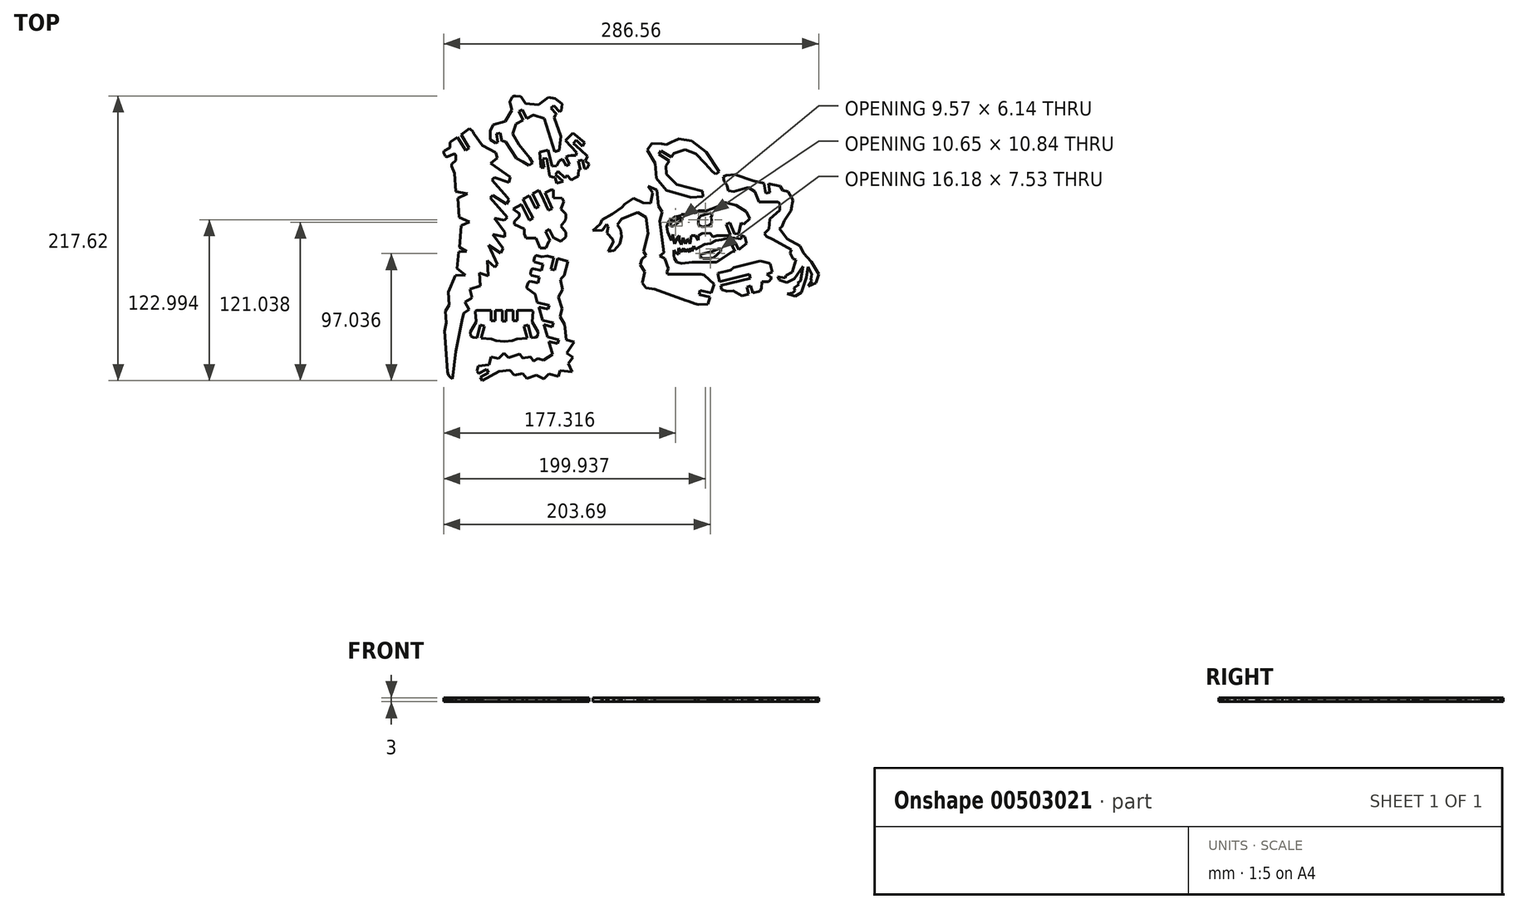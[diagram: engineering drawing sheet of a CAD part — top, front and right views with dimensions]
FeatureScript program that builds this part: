
annotation { "Feature Type Name" : "Feature", "Feature Type Description" : "" }
export const myFeature = defineFeature(function(context is Context, id is Id, definition is map)
    precondition{}
    {
        {
            var Q0;
            Q0=qCreatedBy(makeId("Top.planeOp"),FACE);
            var sketch = newSketch(context, id + "F0", { "sketchPlane" : qUnion([Q0])});
            skLineSegment(sketch, "E0", {"start": v(91.5, -36.51) * mm, "end": v(92.84, -41.9) * mm});
            skLineSegment(sketch, "E1", {"start": v(88.49, -37.26) * mm, "end": v(91.5, -36.51) * mm});
            skLineSegment(sketch, "E2", {"start": v(89.88, -42.83) * mm, "end": v(88.49, -37.26) * mm});
            skLineSegment(sketch, "E3", {"start": v(84.64, -44.14) * mm, "end": v(89.88, -42.83) * mm});
            skLineSegment(sketch, "E4", {"start": v(77.97, -40.13) * mm, "end": v(84.64, -44.14) * mm});
            skLineSegment(sketch, "E5", {"start": v(73.4, -40.63) * mm, "end": v(77.97, -40.13) * mm});
            skLineSegment(sketch, "E6", {"start": v(69.24, -39.21) * mm, "end": v(73.4, -40.63) * mm});
            skLineSegment(sketch, "E7", {"start": v(68.48, -36.17) * mm, "end": v(69.24, -39.21) * mm});
            skLineSegment(sketch, "E8", {"start": v(91.02, -30.55) * mm, "end": v(68.48, -36.17) * mm});
            skLineSegment(sketch, "E9", {"start": v(90.27, -27.54) * mm, "end": v(91.02, -30.55) * mm});
            skLineSegment(sketch, "E10", {"start": v(67.7, -33.17) * mm, "end": v(90.27, -27.54) * mm});
            skLineSegment(sketch, "E11", {"start": v(66.21, -27.25) * mm, "end": v(67.7, -33.17) * mm});
            skLineSegment(sketch, "E12", {"start": v(11.35, -37.86) * mm, "end": v(18.08, -38.98) * mm});
            skLineSegment(sketch, "E13", {"start": v(8.5, -34.14) * mm, "end": v(11.35, -37.86) * mm});
            skLineSegment(sketch, "E14", {"start": v(10.51, -25.54) * mm, "end": v(8.5, -34.14) * mm});
            skLineSegment(sketch, "E15", {"start": v(6.82, -20.1) * mm, "end": v(10.51, -25.54) * mm});
            skLineSegment(sketch, "E16", {"start": v(8.26, -16.25) * mm, "end": v(6.82, -20.1) * mm});
            skLineSegment(sketch, "E17", {"start": v(11.39, -13.12) * mm, "end": v(8.26, -16.25) * mm});
            skLineSegment(sketch, "E18", {"start": v(9.35, -10.1) * mm, "end": v(11.39, -13.12) * mm});
            skLineSegment(sketch, "E19", {"start": v(12.95, 3.58) * mm, "end": v(9.35, -10.1) * mm});
            skLineSegment(sketch, "E20", {"start": v(11.44, 15.91) * mm, "end": v(12.95, 3.58) * mm});
            skLineSegment(sketch, "E21", {"start": v(5.16, 19.64) * mm, "end": v(11.44, 15.91) * mm});
            skLineSegment(sketch, "E22", {"start": v(-7.45, 14.69) * mm, "end": v(5.16, 19.64) * mm});
            skLineSegment(sketch, "E23", {"start": v(-10.52, 10.32) * mm, "end": v(-7.45, 14.69) * mm});
            skLineSegment(sketch, "E24", {"start": v(-7.95, 6.53) * mm, "end": v(-10.52, 10.32) * mm});
            skLineSegment(sketch, "E25", {"start": v(-7.5, 1.3) * mm, "end": v(-7.95, 6.53) * mm});
            skLineSegment(sketch, "E26", {"start": v(-8.77, -4.3) * mm, "end": v(-7.5, 1.3) * mm});
            skLineSegment(sketch, "E27", {"start": v(-13.03, -9.3) * mm, "end": v(-8.77, -4.3) * mm});
            skLineSegment(sketch, "E28", {"start": v(-17.48, -10.2) * mm, "end": v(-13.03, -9.3) * mm});
            skLineSegment(sketch, "E29", {"start": v(-13.87, -3.02) * mm, "end": v(-17.48, -10.2) * mm});
            skLineSegment(sketch, "E30", {"start": v(-14.1, -0.74) * mm, "end": v(-13.87, -3.02) * mm});
            skLineSegment(sketch, "E31", {"start": v(-18.63, 4.02) * mm, "end": v(-14.1, -0.74) * mm});
            skLineSegment(sketch, "E32", {"start": v(-17.58, 8.96) * mm, "end": v(-18.63, 4.02) * mm});
            skLineSegment(sketch, "E33", {"start": v(-18.72, 10.64) * mm, "end": v(-17.58, 8.96) * mm});
            skLineSegment(sketch, "E34", {"start": v(-21.94, 6.01) * mm, "end": v(-18.72, 10.64) * mm});
            skLineSegment(sketch, "E35", {"start": v(-29.34, 5.88) * mm, "end": v(-21.94, 6.01) * mm});
            skLineSegment(sketch, "E36", {"start": v(-23.62, 10.9) * mm, "end": v(-29.34, 5.88) * mm});
            skLineSegment(sketch, "E37", {"start": v(-22.26, 13.94) * mm, "end": v(-23.62, 10.9) * mm});
            skLineSegment(sketch, "E38", {"start": v(-14.4, 18.45) * mm, "end": v(-22.26, 13.94) * mm});
            skLineSegment(sketch, "E39", {"start": v(-7.03, 23.44) * mm, "end": v(-14.4, 18.45) * mm});
            skLineSegment(sketch, "E40", {"start": v(-4.88, 26.04) * mm, "end": v(-7.03, 23.44) * mm});
            skLineSegment(sketch, "E41", {"start": v(1.71, 30.5) * mm, "end": v(-4.88, 26.04) * mm});
            skLineSegment(sketch, "E42", {"start": v(9, 26.97) * mm, "end": v(1.71, 30.5) * mm});
            skLineSegment(sketch, "E43", {"start": v(14.87, 26.71) * mm, "end": v(9, 26.97) * mm});
            skLineSegment(sketch, "E44", {"start": v(16.42, 34.77) * mm, "end": v(14.87, 26.71) * mm});
            skLineSegment(sketch, "E45", {"start": v(13.02, 39.8) * mm, "end": v(16.42, 34.77) * mm});
            skLineSegment(sketch, "E46", {"start": v(19.66, 36.96) * mm, "end": v(13.02, 39.8) * mm});
            skLineSegment(sketch, "E47", {"start": v(20.84, 24.4) * mm, "end": v(19.66, 36.96) * mm});
            skLineSegment(sketch, "E48", {"start": v(23.71, 20.16) * mm, "end": v(20.84, 24.4) * mm});
            skLineSegment(sketch, "E49", {"start": v(21.75, 12.96) * mm, "end": v(23.71, 20.16) * mm});
            skLineSegment(sketch, "E50", {"start": v(25.16, -11.09) * mm, "end": v(21.75, 12.96) * mm});
            skLineSegment(sketch, "E51", {"start": v(21.7, -13.43) * mm, "end": v(25.16, -11.09) * mm});
            skLineSegment(sketch, "E52", {"start": v(25.79, -15.33) * mm, "end": v(21.7, -13.43) * mm});
            skLineSegment(sketch, "E53", {"start": v(28.42, -23.51) * mm, "end": v(25.79, -15.33) * mm});
            skLineSegment(sketch, "E54", {"start": v(27.1, -25.68) * mm, "end": v(28.42, -23.51) * mm});
            skLineSegment(sketch, "E55", {"start": v(27.94, -27.41) * mm, "end": v(27.1, -25.68) * mm});
            skLineSegment(sketch, "E56", {"start": v(53.26, -27.63) * mm, "end": v(27.94, -27.41) * mm});
            skLineSegment(sketch, "E57", {"start": v(66.5, -26.64) * mm, "end": v(66.21, -27.25) * mm});
            skLineSegment(sketch, "E58", {"start": v(78.2, -22.41) * mm, "end": v(75.97, -24.28) * mm});
            skLineSegment(sketch, "E59", {"start": v(98.62, -17.32) * mm, "end": v(78.2, -22.41) * mm});
            skLineSegment(sketch, "E60", {"start": v(105.1, -18.96) * mm, "end": v(98.62, -17.32) * mm});
            skLineSegment(sketch, "E61", {"start": v(106.28, -19.5) * mm, "end": v(105.1, -18.96) * mm});
            skLineSegment(sketch, "E62", {"start": v(107.87, -25.84) * mm, "end": v(106.28, -19.5) * mm});
            skLineSegment(sketch, "E63", {"start": v(103.89, -27.41) * mm, "end": v(107.87, -25.84) * mm});
            skLineSegment(sketch, "E64", {"start": v(107.45, -30.37) * mm, "end": v(103.89, -27.41) * mm});
            skLineSegment(sketch, "E65", {"start": v(105.05, -33.27) * mm, "end": v(107.45, -30.37) * mm});
            skLineSegment(sketch, "E66", {"start": v(100.07, -33.14) * mm, "end": v(105.05, -33.27) * mm});
            skLineSegment(sketch, "E67", {"start": v(99.76, -38.45) * mm, "end": v(100.07, -33.14) * mm});
            skLineSegment(sketch, "E68", {"start": v(98.24, -40.54) * mm, "end": v(99.76, -38.45) * mm});
            skLineSegment(sketch, "E69", {"start": v(92.84, -41.9) * mm, "end": v(98.24, -40.54) * mm});
            skLineSegment(sketch, "E70", {"start": v(-40.32, 47.37) * mm, "end": v(-40.32, 48.76) * mm});
            skLineSegment(sketch, "E71", {"start": v(-49.1, 48.05) * mm, "end": v(-45.64, 44.43) * mm});
            skLineSegment(sketch, "E72", {"start": v(-50.47, 46.1) * mm, "end": v(-49.1, 48.05) * mm});
            skLineSegment(sketch, "E73", {"start": v(-55.93, 51.06) * mm, "end": v(-50.47, 46.1) * mm});
            skLineSegment(sketch, "E74", {"start": v(-58.02, 48.77) * mm, "end": v(-55.93, 51.06) * mm});
            skLineSegment(sketch, "E75", {"start": v(-52.27, 43.55) * mm, "end": v(-58.02, 48.77) * mm});
            skLineSegment(sketch, "E76", {"start": v(-52.48, 43.26) * mm, "end": v(-52.27, 43.55) * mm});
            skLineSegment(sketch, "E77", {"start": v(-57, 42.03) * mm, "end": v(-52.48, 43.26) * mm});
            skLineSegment(sketch, "E78", {"start": v(-58.2, 46.42) * mm, "end": v(-57, 42.03) * mm});
            skLineSegment(sketch, "E79", {"start": v(-59.97, 46.65) * mm, "end": v(-58.2, 46.42) * mm});
            skLineSegment(sketch, "E80", {"start": v(-59.95, 46.62) * mm, "end": v(-59.97, 46.65) * mm});
            skLineSegment(sketch, "E81", {"start": v(-62.16, 47.52) * mm, "end": v(-59.95, 46.62) * mm});
            skLineSegment(sketch, "E82", {"start": v(-64.51, 61.19) * mm, "end": v(-62.16, 47.52) * mm});
            skLineSegment(sketch, "E83", {"start": v(-67.57, 60.67) * mm, "end": v(-64.51, 61.19) * mm});
            skLineSegment(sketch, "E84", {"start": v(-66.45, 54.1) * mm, "end": v(-67.57, 60.67) * mm});
            skLineSegment(sketch, "E85", {"start": v(-69.05, 53.91) * mm, "end": v(-66.45, 54.1) * mm});
            skLineSegment(sketch, "E86", {"start": v(-69.9, 65.77) * mm, "end": v(-69.05, 53.91) * mm});
            skLineSegment(sketch, "E87", {"start": v(-63.55, 67.35) * mm, "end": v(-69.9, 65.77) * mm});
            skLineSegment(sketch, "E88", {"start": v(-60.5, 55.1) * mm, "end": v(-63.55, 67.35) * mm});
            skLineSegment(sketch, "E89", {"start": v(-56.93, 55.35) * mm, "end": v(-60.5, 55.1) * mm});
            skLineSegment(sketch, "E90", {"start": v(-55.15, 59.04) * mm, "end": v(-56.93, 55.35) * mm});
            skLineSegment(sketch, "E91", {"start": v(-52.61, 60.44) * mm, "end": v(-55.15, 59.04) * mm});
            skLineSegment(sketch, "E92", {"start": v(-49.76, 55.27) * mm, "end": v(-52.61, 60.44) * mm});
            skLineSegment(sketch, "E93", {"start": v(-47.05, 56.76) * mm, "end": v(-49.76, 55.27) * mm});
            skLineSegment(sketch, "E94", {"start": v(-49.9, 61.94) * mm, "end": v(-47.05, 56.76) * mm});
            skLineSegment(sketch, "E95", {"start": v(-48.13, 62.91) * mm, "end": v(-49.9, 61.94) * mm});
            skLineSegment(sketch, "E96", {"start": v(-48.13, 62.91) * mm, "end": v(-46.1, 63.33) * mm});
            skLineSegment(sketch, "E97", {"start": v(-42.38, 63.37) * mm, "end": v(-46.1, 63.33) * mm});
            skLineSegment(sketch, "E98", {"start": v(-41.79, 65.42) * mm, "end": v(-42.38, 63.37) * mm});
            skLineSegment(sketch, "E99", {"start": v(-50.23, 74.7) * mm, "end": v(-41.79, 65.42) * mm});
            skLineSegment(sketch, "E100", {"start": v(-44.68, 80.27) * mm, "end": v(-50.23, 74.7) * mm});
            skLineSegment(sketch, "E101", {"start": v(-35.65, 73) * mm, "end": v(-44.68, 80.27) * mm});
            skLineSegment(sketch, "E102", {"start": v(-37.16, 70.38) * mm, "end": v(-35.65, 73) * mm});
            skLineSegment(sketch, "E103", {"start": v(-42, 74.87) * mm, "end": v(-37.16, 70.38) * mm});
            skLineSegment(sketch, "E104", {"start": v(-44.11, 72.6) * mm, "end": v(-42, 74.87) * mm});
            skLineSegment(sketch, "E105", {"start": v(-38.76, 67.64) * mm, "end": v(-44.11, 72.6) * mm});
            skLineSegment(sketch, "E106", {"start": v(-33.5, 62.57) * mm, "end": v(-38.76, 67.64) * mm});
            skLineSegment(sketch, "E107", {"start": v(-34.9, 59.27) * mm, "end": v(-33.5, 62.57) * mm});
            skLineSegment(sketch, "E108", {"start": v(-32.13, 56.54) * mm, "end": v(-34.9, 59.27) * mm});
            skLineSegment(sketch, "E109", {"start": v(-33.8, 53.56) * mm, "end": v(-32.13, 56.54) * mm});
            skLineSegment(sketch, "E110", {"start": v(-35.68, 53) * mm, "end": v(-33.8, 53.56) * mm});
            skLineSegment(sketch, "E111", {"start": v(-37.22, 59.76) * mm, "end": v(-35.68, 53) * mm});
            skLineSegment(sketch, "E112", {"start": v(-40.24, 59.08) * mm, "end": v(-37.22, 59.76) * mm});
            skLineSegment(sketch, "E113", {"start": v(-38.66, 52.13) * mm, "end": v(-40.24, 59.08) * mm});
            skLineSegment(sketch, "E114", {"start": v(-38.75, 52.1) * mm, "end": v(-38.66, 52.13) * mm});
            skLineSegment(sketch, "E115", {"start": v(-40.04, 52.33) * mm, "end": v(-38.75, 52.1) * mm});
            skLineSegment(sketch, "E116", {"start": v(-53.83, 9.3) * mm, "end": v(-50.26, 13.88) * mm});
            skLineSegment(sketch, "E117", {"start": v(-50.05, 4.57) * mm, "end": v(-53.83, 9.3) * mm});
            skLineSegment(sketch, "E118", {"start": v(-50.05, 0.93) * mm, "end": v(-50.05, 4.57) * mm});
            skLineSegment(sketch, "E119", {"start": v(-53.83, -2.31) * mm, "end": v(-50.05, 0.93) * mm});
            skLineSegment(sketch, "E120", {"start": v(-58.95, -0.02) * mm, "end": v(-53.83, -2.31) * mm});
            skLineSegment(sketch, "E121", {"start": v(-59.24, -0.19) * mm, "end": v(-58.95, -0.02) * mm});
            skLineSegment(sketch, "E122", {"start": v(-62.65, 6.68) * mm, "end": v(-59.24, -0.19) * mm});
            skLineSegment(sketch, "E123", {"start": v(-65.43, 5.3) * mm, "end": v(-62.65, 6.68) * mm});
            skLineSegment(sketch, "E124", {"start": v(-61.92, -1.76) * mm, "end": v(-65.43, 5.3) * mm});
            skLineSegment(sketch, "E125", {"start": v(-62.86, -2.31) * mm, "end": v(-61.92, -1.76) * mm});
            skLineSegment(sketch, "E126", {"start": v(-65.16, -7.44) * mm, "end": v(-62.86, -2.31) * mm});
            skLineSegment(sketch, "E127", {"start": v(-69.74, -7.44) * mm, "end": v(-65.16, -7.44) * mm});
            skLineSegment(sketch, "E128", {"start": v(-72.85, -0.02) * mm, "end": v(-69.74, -7.44) * mm});
            skLineSegment(sketch, "E129", {"start": v(-81.75, 3.35) * mm, "end": v(-80.53, -0.02) * mm});
            skLineSegment(sketch, "E130", {"start": v(-81.75, 7.13) * mm, "end": v(-81.75, 3.35) * mm});
            skLineSegment(sketch, "E131", {"start": v(-95.51, -63.25) * mm, "end": v(-98.62, -63.25) * mm});
            skLineSegment(sketch, "E132", {"start": v(-95.51, -55.05) * mm, "end": v(-95.51, -63.25) * mm});
            skLineSegment(sketch, "E133", {"start": v(-90.16, -55.05) * mm, "end": v(-95.51, -55.05) * mm});
            skLineSegment(sketch, "E134", {"start": v(-90.16, -63.23) * mm, "end": v(-90.16, -55.05) * mm});
            skLineSegment(sketch, "E135", {"start": v(-87.05, -63.23) * mm, "end": v(-90.16, -63.23) * mm});
            skLineSegment(sketch, "E136", {"start": v(-87.05, -55.05) * mm, "end": v(-87.05, -63.23) * mm});
            skLineSegment(sketch, "E137", {"start": v(-76.28, -55.05) * mm, "end": v(-87.05, -55.05) * mm});
            skLineSegment(sketch, "E138", {"start": v(-75.04, -55.83) * mm, "end": v(-76.28, -55.05) * mm});
            skLineSegment(sketch, "E139", {"start": v(-75.48, -63.94) * mm, "end": v(-75.04, -55.83) * mm});
            skLineSegment(sketch, "E140", {"start": v(-71.21, -71.63) * mm, "end": v(-75.48, -63.94) * mm});
            skLineSegment(sketch, "E141", {"start": v(-71.65, -74.71) * mm, "end": v(-71.21, -71.63) * mm});
            skLineSegment(sketch, "E142", {"start": v(-73.26, -75.84) * mm, "end": v(-71.65, -74.71) * mm});
            skLineSegment(sketch, "E143", {"start": v(-76.36, -76.12) * mm, "end": v(-73.26, -75.84) * mm});
            skLineSegment(sketch, "E144", {"start": v(-78.83, -66.37) * mm, "end": v(-76.36, -76.12) * mm});
            skLineSegment(sketch, "E145", {"start": v(-81.84, -67.13) * mm, "end": v(-78.83, -66.37) * mm});
            skLineSegment(sketch, "E146", {"start": v(-79.48, -76.4) * mm, "end": v(-81.84, -67.13) * mm});
            skLineSegment(sketch, "E147", {"start": v(-87.36, -77.1) * mm, "end": v(-79.48, -76.4) * mm});
            skLineSegment(sketch, "E148", {"start": v(-89.17, 10.64) * mm, "end": v(-81.75, 7.13) * mm});
            skLineSegment(sketch, "E149", {"start": v(-89.17, 12.66) * mm, "end": v(-89.17, 10.64) * mm});
            skLineSegment(sketch, "E150", {"start": v(-85.39, 16.57) * mm, "end": v(-89.17, 12.66) * mm});
            skLineSegment(sketch, "E151", {"start": v(-85.39, 18.87) * mm, "end": v(-85.39, 16.57) * mm});
            skLineSegment(sketch, "E152", {"start": v(-90.38, 22.24) * mm, "end": v(-85.39, 18.87) * mm});
            skLineSegment(sketch, "E153", {"start": v(-83.99, 25.73) * mm, "end": v(-90.38, 22.24) * mm});
            skLineSegment(sketch, "E154", {"start": v(-77.85, 13.83) * mm, "end": v(-83.99, 25.73) * mm});
            skLineSegment(sketch, "E155", {"start": v(-75.1, 15.25) * mm, "end": v(-77.85, 13.83) * mm});
            skLineSegment(sketch, "E156", {"start": v(-81.27, 27.22) * mm, "end": v(-75.1, 15.25) * mm});
            skLineSegment(sketch, "E157", {"start": v(-82.76, 29.95) * mm, "end": v(-81.27, 27.22) * mm});
            skLineSegment(sketch, "E158", {"start": v(-77.93, 32.6) * mm, "end": v(-82.76, 29.95) * mm});
            skLineSegment(sketch, "E159", {"start": v(-73.19, 22.97) * mm, "end": v(-77.93, 32.6) * mm});
            skLineSegment(sketch, "E160", {"start": v(-70.4, 24.34) * mm, "end": v(-73.19, 22.97) * mm});
            skLineSegment(sketch, "E161", {"start": v(-75.2, 34.09) * mm, "end": v(-70.4, 24.34) * mm});
            skLineSegment(sketch, "E162", {"start": v(-70.59, 36.61) * mm, "end": v(-75.2, 34.09) * mm});
            skLineSegment(sketch, "E163", {"start": v(-68.67, 33.1) * mm, "end": v(-70.59, 36.61) * mm});
            skLineSegment(sketch, "E164", {"start": v(-63.22, 21.21) * mm, "end": v(-68.67, 33.1) * mm});
            skLineSegment(sketch, "E165", {"start": v(-60.4, 22.5) * mm, "end": v(-63.22, 21.21) * mm});
            skLineSegment(sketch, "E166", {"start": v(-65.94, 34.59) * mm, "end": v(-60.4, 22.5) * mm});
            skLineSegment(sketch, "E167", {"start": v(-61.45, 37.04) * mm, "end": v(-65.94, 34.59) * mm});
            skLineSegment(sketch, "E168", {"start": v(-59.5, 37.04) * mm, "end": v(-61.45, 37.04) * mm});
            skLineSegment(sketch, "E169", {"start": v(-59.5, 31) * mm, "end": v(-59.5, 37.04) * mm});
            skLineSegment(sketch, "E170", {"start": v(-52.88, 30.6) * mm, "end": v(-59.5, 31) * mm});
            skLineSegment(sketch, "E171", {"start": v(-51.4, 27.9) * mm, "end": v(-52.88, 30.6) * mm});
            skLineSegment(sketch, "E172", {"start": v(-50.05, 18.6) * mm, "end": v(-53.83, 22.37) * mm});
            skLineSegment(sketch, "E173", {"start": v(-50.05, 16.1) * mm, "end": v(-50.05, 18.6) * mm});
            skLineSegment(sketch, "E174", {"start": v(122.4, -8.86) * mm, "end": v(121.6, -11.43) * mm});
            skLineSegment(sketch, "E175", {"start": v(108.16, -1) * mm, "end": v(122.4, -8.86) * mm});
            skLineSegment(sketch, "E176", {"start": v(103.31, 1.25) * mm, "end": v(108.16, -1) * mm});
            skLineSegment(sketch, "E177", {"start": v(101.98, 3.56) * mm, "end": v(103.31, 1.25) * mm});
            skLineSegment(sketch, "E178", {"start": v(105.23, 7.2) * mm, "end": v(101.98, 3.56) * mm});
            skLineSegment(sketch, "E179", {"start": v(105.81, 14.67) * mm, "end": v(105.23, 7.2) * mm});
            skLineSegment(sketch, "E180", {"start": v(113.73, 21.48) * mm, "end": v(105.81, 14.67) * mm});
            skLineSegment(sketch, "E181", {"start": v(113.63, 26.45) * mm, "end": v(113.73, 21.48) * mm});
            skLineSegment(sketch, "E182", {"start": v(112.42, 27.72) * mm, "end": v(113.63, 26.45) * mm});
            skLineSegment(sketch, "E183", {"start": v(97.73, 27.84) * mm, "end": v(112.42, 27.72) * mm});
            skLineSegment(sketch, "E184", {"start": v(102.92, 34.46) * mm, "end": v(105.98, 34.97) * mm});
            skLineSegment(sketch, "E185", {"start": v(-89.68, 108.64) * mm, "end": v(-90.25, 108.36) * mm});
            skLineSegment(sketch, "E186", {"start": v(-89.06, 108.81) * mm, "end": v(-89.68, 108.64) * mm});
            skLineSegment(sketch, "E187", {"start": v(-88.42, 108.68) * mm, "end": v(-89.06, 108.81) * mm});
            skLineSegment(sketch, "E188", {"start": v(-84.61, 108.24) * mm, "end": v(-88.42, 108.68) * mm});
            skLineSegment(sketch, "E189", {"start": v(-84.21, 107.97) * mm, "end": v(-84.61, 108.24) * mm});
            skLineSegment(sketch, "E190", {"start": v(-83.93, 107.57) * mm, "end": v(-84.21, 107.97) * mm});
            skLineSegment(sketch, "E191", {"start": v(-80.83, 102.96) * mm, "end": v(-83.93, 107.57) * mm});
            skLineSegment(sketch, "E192", {"start": v(-70.9, 102) * mm, "end": v(-80.83, 102.96) * mm});
            skLineSegment(sketch, "E193", {"start": v(-59.22, 101.52) * mm, "end": v(-61.49, 99.4) * mm});
            skLineSegment(sketch, "E194", {"start": v(-54.48, 103.9) * mm, "end": v(-58.15, 106.62) * mm});
            skLineSegment(sketch, "E195", {"start": v(-53.38, 97.7) * mm, "end": v(-52.85, 102.69) * mm});
            skLineSegment(sketch, "E196", {"start": v(-57.72, 94.48) * mm, "end": v(-57.23, 94.84) * mm});
            skLineSegment(sketch, "E197", {"start": v(-58.81, 92.13) * mm, "end": v(-57.72, 94.48) * mm});
            skLineSegment(sketch, "E198", {"start": v(36.44, 76.04) * mm, "end": v(46.32, 74.24) * mm});
            skLineSegment(sketch, "E199", {"start": v(46.32, 74.24) * mm, "end": v(57.28, 65.88) * mm});
            skLineSegment(sketch, "E200", {"start": v(67.26, 51) * mm, "end": v(57.28, 65.88) * mm});
            skLineSegment(sketch, "E201", {"start": v(64.6, 48.91) * mm, "end": v(67.26, 51) * mm});
            skLineSegment(sketch, "E202", {"start": v(62.1, 50.83) * mm, "end": v(64.6, 48.91) * mm});
            skLineSegment(sketch, "E203", {"start": v(56.57, 57.27) * mm, "end": v(62.1, 50.83) * mm});
            skLineSegment(sketch, "E204", {"start": v(49.55, 64.5) * mm, "end": v(56.57, 57.27) * mm});
            skLineSegment(sketch, "E205", {"start": v(41.34, 67.72) * mm, "end": v(49.55, 64.5) * mm});
            skLineSegment(sketch, "E206", {"start": v(32.54, 64.95) * mm, "end": v(41.34, 67.72) * mm});
            skLineSegment(sketch, "E207", {"start": v(30.64, 61.92) * mm, "end": v(32.54, 64.95) * mm});
            skLineSegment(sketch, "E208", {"start": v(22.94, 66.76) * mm, "end": v(30.64, 61.92) * mm});
            skLineSegment(sketch, "E209", {"start": v(21.29, 64.14) * mm, "end": v(22.94, 66.76) * mm});
            skLineSegment(sketch, "E210", {"start": v(28.99, 59.3) * mm, "end": v(21.29, 64.14) * mm});
            skLineSegment(sketch, "E211", {"start": v(26.51, 55.36) * mm, "end": v(28.99, 59.3) * mm});
            skLineSegment(sketch, "E212", {"start": v(27.04, 48.98) * mm, "end": v(26.51, 55.36) * mm});
            skLineSegment(sketch, "E213", {"start": v(34.95, 41.07) * mm, "end": v(27.04, 48.98) * mm});
            skLineSegment(sketch, "E214", {"start": v(54.59, 36) * mm, "end": v(34.95, 41.07) * mm});
            skLineSegment(sketch, "E215", {"start": v(54.89, 31.77) * mm, "end": v(54.59, 36) * mm});
            skLineSegment(sketch, "E216", {"start": v(45.66, 31.14) * mm, "end": v(54.89, 31.77) * mm});
            skLineSegment(sketch, "E217", {"start": v(26.77, 36.65) * mm, "end": v(45.66, 31.14) * mm});
            skLineSegment(sketch, "E218", {"start": v(19.16, 45.73) * mm, "end": v(26.77, 36.65) * mm});
            skLineSegment(sketch, "E219", {"start": v(18.4, 57.33) * mm, "end": v(19.16, 45.73) * mm});
            skLineSegment(sketch, "E220", {"start": v(12.39, 67.49) * mm, "end": v(18.4, 57.33) * mm});
            skLineSegment(sketch, "E221", {"start": v(15.7, 72.51) * mm, "end": v(12.39, 67.49) * mm});
            skLineSegment(sketch, "E222", {"start": v(23.45, 72.05) * mm, "end": v(15.7, 72.51) * mm});
            skLineSegment(sketch, "E223", {"start": v(-53.75, 77.9) * mm, "end": v(-58.81, 92.13) * mm});
            skLineSegment(sketch, "E224", {"start": v(-55.12, 67.1) * mm, "end": v(-53.75, 77.9) * mm});
            skLineSegment(sketch, "E225", {"start": v(-58.37, 66) * mm, "end": v(-55.12, 67.1) * mm});
            skLineSegment(sketch, "E226", {"start": v(-74.91, 93.93) * mm, "end": v(-74.24, 94.08) * mm});
            skLineSegment(sketch, "E227", {"start": v(-79.87, 91.63) * mm, "end": v(-74.91, 93.93) * mm});
            skLineSegment(sketch, "E228", {"start": v(-83.17, 98.27) * mm, "end": v(-79.87, 91.63) * mm});
            skLineSegment(sketch, "E229", {"start": v(94.59, 35.58) * mm, "end": v(97.73, 27.84) * mm});
            skLineSegment(sketch, "E230", {"start": v(89.5, 38.72) * mm, "end": v(94.59, 35.58) * mm});
            skLineSegment(sketch, "E231", {"start": v(78.35, 35.58) * mm, "end": v(89.5, 38.72) * mm});
            skLineSegment(sketch, "E232", {"start": v(73.4, 40.45) * mm, "end": v(74.12, 36.16) * mm});
            skLineSegment(sketch, "E233", {"start": v(-93.53, 42.69) * mm, "end": v(-92.32, 46.63) * mm});
            skLineSegment(sketch, "E234", {"start": v(-104.44, 46.56) * mm, "end": v(-93.53, 42.69) * mm});
            skLineSegment(sketch, "E235", {"start": v(-106.5, 44.53) * mm, "end": v(-104.44, 46.56) * mm});
            skLineSegment(sketch, "E236", {"start": v(-94.8, 31.36) * mm, "end": v(-106.5, 44.53) * mm});
            skLineSegment(sketch, "E237", {"start": v(-95.24, 26.04) * mm, "end": v(-93.45, 29.23) * mm});
            skLineSegment(sketch, "E238", {"start": v(-105.73, 32.84) * mm, "end": v(-95.24, 26.04) * mm});
            skLineSegment(sketch, "E239", {"start": v(-107.6, 30.94) * mm, "end": v(-105.73, 32.84) * mm});
            skLineSegment(sketch, "E240", {"start": v(-94.58, 16.08) * mm, "end": v(-107.6, 30.94) * mm});
            skLineSegment(sketch, "E241", {"start": v(-96.76, 13.87) * mm, "end": v(-94.58, 16.08) * mm});
            skLineSegment(sketch, "E242", {"start": v(-104.59, 15.32) * mm, "end": v(-96.76, 13.87) * mm});
            skLineSegment(sketch, "E243", {"start": v(-96.68, 4.47) * mm, "end": v(-104.59, 15.32) * mm});
            skLineSegment(sketch, "E244", {"start": v(-96.45, 1.07) * mm, "end": v(-96.68, 4.47) * mm});
            skLineSegment(sketch, "E245", {"start": v(-105.77, 2.94) * mm, "end": v(-96.45, 1.07) * mm});
            skLineSegment(sketch, "E246", {"start": v(-97.78, -7.99) * mm, "end": v(-105.77, 2.94) * mm});
            skLineSegment(sketch, "E247", {"start": v(-99.76, -11.39) * mm, "end": v(-97.78, -7.99) * mm});
            skLineSegment(sketch, "E248", {"start": v(-108.83, -5.25) * mm, "end": v(-99.76, -11.39) * mm});
            skLineSegment(sketch, "E249", {"start": v(-102.29, -19.82) * mm, "end": v(-108.83, -5.25) * mm});
            skLineSegment(sketch, "E250", {"start": v(-104.13, -22.19) * mm, "end": v(-102.29, -19.82) * mm});
            skLineSegment(sketch, "E251", {"start": v(-109.96, -16.94) * mm, "end": v(-104.13, -22.19) * mm});
            skLineSegment(sketch, "E252", {"start": v(-109.2, -28.71) * mm, "end": v(-109.96, -16.94) * mm});
            skLineSegment(sketch, "E253", {"start": v(-115.82, -26.49) * mm, "end": v(-109.2, -28.71) * mm});
            skLineSegment(sketch, "E254", {"start": v(-115.18, -36.28) * mm, "end": v(-115.82, -26.49) * mm});
            skLineSegment(sketch, "E255", {"start": v(-123.32, -38.89) * mm, "end": v(-115.18, -36.28) * mm});
            skLineSegment(sketch, "E256", {"start": v(-121.55, -45.3) * mm, "end": v(-123.32, -38.89) * mm});
            skLineSegment(sketch, "E257", {"start": v(-127.1, -48.96) * mm, "end": v(-122.8, -46.4) * mm});
            skLineSegment(sketch, "E258", {"start": v(-124, -54.4) * mm, "end": v(-127.1, -48.96) * mm});
            skLineSegment(sketch, "E259", {"start": v(-128.02, -57.45) * mm, "end": v(-124, -54.4) * mm});
            skLineSegment(sketch, "E260", {"start": v(-129.31, -62.86) * mm, "end": v(-128.02, -57.45) * mm});
            skLineSegment(sketch, "E261", {"start": v(-134.01, -86.43) * mm, "end": v(-129.31, -62.86) * mm});
            skLineSegment(sketch, "E262", {"start": v(-136.48, -107.48) * mm, "end": v(-134.01, -86.43) * mm});
            skLineSegment(sketch, "E263", {"start": v(-137.43, -106.96) * mm, "end": v(-136.48, -107.48) * mm});
            skLineSegment(sketch, "E264", {"start": v(-138.63, -106.08) * mm, "end": v(-137.43, -106.96) * mm});
            skLineSegment(sketch, "E265", {"start": v(-139.59, -104.9) * mm, "end": v(-138.63, -106.08) * mm});
            skLineSegment(sketch, "E266", {"start": v(-140.23, -103.5) * mm, "end": v(-139.59, -104.9) * mm});
            skLineSegment(sketch, "E267", {"start": v(-140.52, -101.97) * mm, "end": v(-140.23, -103.5) * mm});
            skLineSegment(sketch, "E268", {"start": v(-142.54, -71) * mm, "end": v(-140.52, -101.97) * mm});
            skLineSegment(sketch, "E269", {"start": v(-141.27, -64.82) * mm, "end": v(-142.54, -71) * mm});
            skLineSegment(sketch, "E270", {"start": v(-141.86, -55.76) * mm, "end": v(-141.27, -64.82) * mm});
            skLineSegment(sketch, "E271", {"start": v(-139, -50.91) * mm, "end": v(-141.86, -55.76) * mm});
            skLineSegment(sketch, "E272", {"start": v(-139, -50.91) * mm, "end": v(-139.62, -41.24) * mm});
            skLineSegment(sketch, "E273", {"start": v(-139.62, -41.24) * mm, "end": v(-134.3, -28.59) * mm});
            skLineSegment(sketch, "E274", {"start": v(-134.3, -28.59) * mm, "end": v(-126.62, -28) * mm});
            skLineSegment(sketch, "E275", {"start": v(-126.62, -28) * mm, "end": v(-133.13, -23.17) * mm});
            skLineSegment(sketch, "E276", {"start": v(-133.13, -23.17) * mm, "end": v(-131.71, -10.45) * mm});
            skLineSegment(sketch, "E277", {"start": v(-131.71, -10.45) * mm, "end": v(-125.92, -10.01) * mm});
            skLineSegment(sketch, "E278", {"start": v(-125.92, -10.01) * mm, "end": v(-131.08, -6.92) * mm});
            skLineSegment(sketch, "E279", {"start": v(-131.08, -6.92) * mm, "end": v(-129.91, 9.73) * mm});
            skLineSegment(sketch, "E280", {"start": v(-129.91, 9.73) * mm, "end": v(-123.66, 12.33) * mm});
            skLineSegment(sketch, "E281", {"start": v(-123.66, 12.33) * mm, "end": v(-131.41, 15.82) * mm});
            skLineSegment(sketch, "E282", {"start": v(-131.41, 15.82) * mm, "end": v(-132.37, 30.43) * mm});
            skLineSegment(sketch, "E283", {"start": v(-132.37, 30.43) * mm, "end": v(-125.14, 34.12) * mm});
            skLineSegment(sketch, "E284", {"start": v(-125.14, 34.12) * mm, "end": v(-134.1, 35.68) * mm});
            skLineSegment(sketch, "E285", {"start": v(-135.02, 49.65) * mm, "end": v(-134.1, 35.68) * mm});
            skLineSegment(sketch, "E286", {"start": v(-137.16, 55.05) * mm, "end": v(-135.02, 49.65) * mm});
            skLineSegment(sketch, "E287", {"start": v(-137.27, 55.66) * mm, "end": v(-137.16, 55.05) * mm});
            skLineSegment(sketch, "E288", {"start": v(-137.14, 56.27) * mm, "end": v(-137.27, 55.66) * mm});
            skLineSegment(sketch, "E289", {"start": v(-136.8, 56.78) * mm, "end": v(-137.14, 56.27) * mm});
            skLineSegment(sketch, "E290", {"start": v(-134.44, 59.02) * mm, "end": v(-136.8, 56.78) * mm});
            skLineSegment(sketch, "E291", {"start": v(-134.06, 59.58) * mm, "end": v(-134.44, 59.02) * mm});
            skLineSegment(sketch, "E292", {"start": v(-133.96, 60.26) * mm, "end": v(-134.06, 59.58) * mm});
            skLineSegment(sketch, "E293", {"start": v(-134.15, 63.08) * mm, "end": v(-133.96, 60.26) * mm});
            skLineSegment(sketch, "E294", {"start": v(-134.35, 63.77) * mm, "end": v(-134.15, 63.08) * mm});
            skLineSegment(sketch, "E295", {"start": v(-134.82, 64.27) * mm, "end": v(-134.35, 63.77) * mm});
            skLineSegment(sketch, "E296", {"start": v(-135.45, 64.5) * mm, "end": v(-134.82, 64.27) * mm});
            skLineSegment(sketch, "E297", {"start": v(-136.1, 64.37) * mm, "end": v(-135.45, 64.5) * mm});
            skLineSegment(sketch, "E298", {"start": v(-140.54, 62.33) * mm, "end": v(-136.1, 64.37) * mm});
            skLineSegment(sketch, "E299", {"start": v(-141.27, 62.22) * mm, "end": v(-140.54, 62.33) * mm});
            skLineSegment(sketch, "E300", {"start": v(-141.94, 62.51) * mm, "end": v(-141.27, 62.22) * mm});
            skLineSegment(sketch, "E301", {"start": v(-142.4, 63.13) * mm, "end": v(-141.94, 62.51) * mm});
            skLineSegment(sketch, "E302", {"start": v(-143.18, 65.11) * mm, "end": v(-142.4, 63.13) * mm});
            skLineSegment(sketch, "E303", {"start": v(-143.28, 65.89) * mm, "end": v(-143.18, 65.11) * mm});
            skLineSegment(sketch, "E304", {"start": v(-143, 66.62) * mm, "end": v(-143.28, 65.89) * mm});
            skLineSegment(sketch, "E305", {"start": v(-142.44, 67.1) * mm, "end": v(-143, 66.62) * mm});
            skLineSegment(sketch, "E306", {"start": v(-139.32, 68.53) * mm, "end": v(-142.44, 67.1) * mm});
            skLineSegment(sketch, "E307", {"start": v(-138.85, 68.89) * mm, "end": v(-139.32, 68.53) * mm});
            skLineSegment(sketch, "E308", {"start": v(-138.55, 69.42) * mm, "end": v(-138.85, 68.89) * mm});
            skLineSegment(sketch, "E309", {"start": v(-138.47, 70.04) * mm, "end": v(-138.55, 69.42) * mm});
            skLineSegment(sketch, "E310", {"start": v(-138.6, 72.16) * mm, "end": v(-138.47, 70.04) * mm});
            skLineSegment(sketch, "E311", {"start": v(-138.53, 72.79) * mm, "end": v(-138.6, 72.16) * mm});
            skLineSegment(sketch, "E312", {"start": v(-138.22, 73.32) * mm, "end": v(-138.53, 72.79) * mm});
            skLineSegment(sketch, "E313", {"start": v(-137.73, 73.67) * mm, "end": v(-138.22, 73.32) * mm});
            skLineSegment(sketch, "E314", {"start": v(-132.65, 77.29) * mm, "end": v(-137.73, 73.67) * mm});
            skLineSegment(sketch, "E315", {"start": v(-126.46, 67.2) * mm, "end": v(-132.65, 77.29) * mm});
            skLineSegment(sketch, "E316", {"start": v(-123.88, 69.03) * mm, "end": v(-126.46, 67.2) * mm});
            skLineSegment(sketch, "E317", {"start": v(-130.06, 79.13) * mm, "end": v(-123.88, 69.03) * mm});
            skLineSegment(sketch, "E318", {"start": v(-123.73, 84) * mm, "end": v(-130.06, 79.13) * mm});
            skLineSegment(sketch, "E319", {"start": v(-123.73, 84) * mm, "end": v(-122.51, 83.04) * mm});
            skLineSegment(sketch, "E320", {"start": v(-121.39, 81.9) * mm, "end": v(-122.51, 83.04) * mm});
            skLineSegment(sketch, "E321", {"start": v(-120.76, 80.97) * mm, "end": v(-121.39, 81.9) * mm});
            skLineSegment(sketch, "E322", {"start": v(-120.26, 80.13) * mm, "end": v(-120.76, 80.97) * mm});
            skLineSegment(sketch, "E323", {"start": v(-113.66, 70.98) * mm, "end": v(-120.26, 80.13) * mm});
            skLineSegment(sketch, "E324", {"start": v(-103.46, 65.47) * mm, "end": v(-113.66, 70.98) * mm});
            skLineSegment(sketch, "E325", {"start": v(-102.32, 61.36) * mm, "end": v(-103.46, 65.47) * mm});
            skLineSegment(sketch, "E326", {"start": v(-107.33, 57.25) * mm, "end": v(-102.32, 61.36) * mm});
            skLineSegment(sketch, "E327", {"start": v(-92.32, 46.63) * mm, "end": v(-107.33, 57.25) * mm});
            skLineSegment(sketch, "E328", {"start": v(71.03, 43.62) * mm, "end": v(73.4, 40.45) * mm});
            skLineSegment(sketch, "E329", {"start": v(70.43, 47.22) * mm, "end": v(71.03, 43.62) * mm});
            skLineSegment(sketch, "E330", {"start": v(79.16, 48.68) * mm, "end": v(72.66, 47.93) * mm});
            skLineSegment(sketch, "E331", {"start": v(93.23, 43.75) * mm, "end": v(79.16, 48.68) * mm});
            skLineSegment(sketch, "E332", {"start": v(113.94, 39.82) * mm, "end": v(104.89, 41.54) * mm});
            skLineSegment(sketch, "E333", {"start": v(115.86, 36.5) * mm, "end": v(113.94, 39.82) * mm});
            skLineSegment(sketch, "E334", {"start": v(120.1, 35.72) * mm, "end": v(115.86, 36.5) * mm});
            skLineSegment(sketch, "E335", {"start": v(117.15, 13.43) * mm, "end": v(122.2, 21.13) * mm});
            skLineSegment(sketch, "E336", {"start": v(115.17, 8.54) * mm, "end": v(117.15, 13.43) * mm});
            skLineSegment(sketch, "E337", {"start": v(113.12, 7.36) * mm, "end": v(115.17, 8.54) * mm});
            skLineSegment(sketch, "E338", {"start": v(119.25, -0.4) * mm, "end": v(113.12, 7.36) * mm});
            skLineSegment(sketch, "E339", {"start": v(131.84, -11.18) * mm, "end": v(129.2, -6.01) * mm});
            skLineSegment(sketch, "E340", {"start": v(137.87, -18.1) * mm, "end": v(131.84, -11.18) * mm});
            skLineSegment(sketch, "E341", {"start": v(143.28, -27.65) * mm, "end": v(137.87, -18.1) * mm});
            skLineSegment(sketch, "E342", {"start": v(141.13, -34.28) * mm, "end": v(143.28, -27.65) * mm});
            skLineSegment(sketch, "E343", {"start": v(135.6, -36.74) * mm, "end": v(141.13, -34.28) * mm});
            skLineSegment(sketch, "E344", {"start": v(138.03, -32.56) * mm, "end": v(135.6, -36.74) * mm});
            skLineSegment(sketch, "E345", {"start": v(137.41, -31.18) * mm, "end": v(138.03, -32.56) * mm});
            skLineSegment(sketch, "E346", {"start": v(137.88, -27.55) * mm, "end": v(137.41, -31.18) * mm});
            skLineSegment(sketch, "E347", {"start": v(135.05, -21.67) * mm, "end": v(137.88, -27.55) * mm});
            skLineSegment(sketch, "E348", {"start": v(133.99, -30.07) * mm, "end": v(135.05, -21.67) * mm});
            skLineSegment(sketch, "E349", {"start": v(130.25, -41.62) * mm, "end": v(133.99, -30.07) * mm});
            skLineSegment(sketch, "E350", {"start": v(119.24, -42.43) * mm, "end": v(125.22, -44.36) * mm});
            skLineSegment(sketch, "E351", {"start": v(123.3, -41.85) * mm, "end": v(119.24, -42.43) * mm});
            skLineSegment(sketch, "E352", {"start": v(125.22, -40) * mm, "end": v(123.3, -41.85) * mm});
            skLineSegment(sketch, "E353", {"start": v(124.54, -38.04) * mm, "end": v(125.22, -40) * mm});
            skLineSegment(sketch, "E354", {"start": v(128.05, -35.6) * mm, "end": v(124.54, -38.04) * mm});
            skLineSegment(sketch, "E355", {"start": v(127.1, -34.22) * mm, "end": v(128.05, -35.6) * mm});
            skLineSegment(sketch, "E356", {"start": v(129.53, -32.53) * mm, "end": v(127.1, -34.22) * mm});
            skLineSegment(sketch, "E357", {"start": v(131.21, -21.5) * mm, "end": v(129.53, -32.53) * mm});
            skLineSegment(sketch, "E358", {"start": v(124.83, -31) * mm, "end": v(131.21, -21.5) * mm});
            skLineSegment(sketch, "E359", {"start": v(118.84, -33.8) * mm, "end": v(124.83, -31) * mm});
            skLineSegment(sketch, "E360", {"start": v(113.39, -32.02) * mm, "end": v(118.84, -33.8) * mm});
            skLineSegment(sketch, "E361", {"start": v(112.12, -29.37) * mm, "end": v(113.39, -32.02) * mm});
            skLineSegment(sketch, "E362", {"start": v(117.65, -30.36) * mm, "end": v(112.12, -29.37) * mm});
            skLineSegment(sketch, "E363", {"start": v(118.21, -28.62) * mm, "end": v(117.65, -30.36) * mm});
            skLineSegment(sketch, "E364", {"start": v(123.12, -25.78) * mm, "end": v(118.21, -28.62) * mm});
            skLineSegment(sketch, "E365", {"start": v(126.1, -16.56) * mm, "end": v(123.12, -25.78) * mm});
            skLineSegment(sketch, "E366", {"start": v(123.83, -15.82) * mm, "end": v(126.1, -16.56) * mm});
            skLineSegment(sketch, "E367", {"start": v(121.6, -11.43) * mm, "end": v(123.83, -15.82) * mm});
            skLineSegment(sketch, "E368", {"start": v(63.46, -35.23) * mm, "end": v(55.73, -28.2) * mm});
            skLineSegment(sketch, "E369", {"start": v(-76.06, -23.64) * mm, "end": v(-76.26, -23.9) * mm});
            skLineSegment(sketch, "E370", {"start": v(-75.43, -23.27) * mm, "end": v(-76.06, -23.64) * mm});
            skLineSegment(sketch, "E371", {"start": v(-74.7, -23.26) * mm, "end": v(-75.43, -23.27) * mm});
            skLineSegment(sketch, "E372", {"start": v(-68.8, -24.79) * mm, "end": v(-74.7, -23.26) * mm});
            skLineSegment(sketch, "E373", {"start": v(-67.55, -19.94) * mm, "end": v(-68.8, -24.79) * mm});
            skLineSegment(sketch, "E374", {"start": v(-73.45, -18.42) * mm, "end": v(-67.55, -19.94) * mm});
            skLineSegment(sketch, "E375", {"start": v(-74.09, -18.06) * mm, "end": v(-73.45, -18.42) * mm});
            skLineSegment(sketch, "E376", {"start": v(-74.46, -17.43) * mm, "end": v(-74.09, -18.06) * mm});
            skLineSegment(sketch, "E377", {"start": v(-74.46, -16.7) * mm, "end": v(-74.46, -17.43) * mm});
            skLineSegment(sketch, "E378", {"start": v(-73.86, -14.36) * mm, "end": v(-74.46, -16.7) * mm});
            skLineSegment(sketch, "E379", {"start": v(-73.5, -13.73) * mm, "end": v(-73.86, -14.36) * mm});
            skLineSegment(sketch, "E380", {"start": v(-72.87, -13.36) * mm, "end": v(-73.5, -13.73) * mm});
            skLineSegment(sketch, "E381", {"start": v(-72.14, -13.35) * mm, "end": v(-72.87, -13.36) * mm});
            skLineSegment(sketch, "E382", {"start": v(-68.44, -14.3) * mm, "end": v(-72.14, -13.35) * mm});
            skLineSegment(sketch, "E383", {"start": v(-59.1, -14.84) * mm, "end": v(-64.24, -13.51) * mm});
            skLineSegment(sketch, "E384", {"start": v(-61.36, -23.58) * mm, "end": v(-59.1, -14.84) * mm});
            skLineSegment(sketch, "E385", {"start": v(-58.36, -24.36) * mm, "end": v(-61.36, -23.58) * mm});
            skLineSegment(sketch, "E386", {"start": v(-56.1, -15.61) * mm, "end": v(-58.36, -24.36) * mm});
            skLineSegment(sketch, "E387", {"start": v(-51.22, -28.62) * mm, "end": v(-48.38, -17.6) * mm});
            skLineSegment(sketch, "E388", {"start": v(-52.82, -29.96) * mm, "end": v(-51.22, -28.62) * mm});
            skLineSegment(sketch, "E389", {"start": v(-52.57, -39.31) * mm, "end": v(-54.12, -31.66) * mm});
            skLineSegment(sketch, "E390", {"start": v(-55.7, -45.08) * mm, "end": v(-52.57, -39.31) * mm});
            skLineSegment(sketch, "E391", {"start": v(-52.8, -53.82) * mm, "end": v(-55.7, -45.08) * mm});
            skLineSegment(sketch, "E392", {"start": v(-54.39, -60) * mm, "end": v(-52.8, -53.82) * mm});
            skLineSegment(sketch, "E393", {"start": v(-50.95, -65.8) * mm, "end": v(-54.39, -60) * mm});
            skLineSegment(sketch, "E394", {"start": v(-49.69, -77.79) * mm, "end": v(-50.95, -65.8) * mm});
            skLineSegment(sketch, "E395", {"start": v(-43.58, -79.36) * mm, "end": v(-49.69, -77.79) * mm});
            skLineSegment(sketch, "E396", {"start": v(-49.28, -87.72) * mm, "end": v(-43.58, -79.36) * mm});
            skLineSegment(sketch, "E397", {"start": v(-44.52, -90.96) * mm, "end": v(-49.28, -87.72) * mm});
            skLineSegment(sketch, "E398", {"start": v(-47.85, -95.84) * mm, "end": v(-44.52, -90.96) * mm});
            skLineSegment(sketch, "E399", {"start": v(-45.05, -102.1) * mm, "end": v(-47.85, -95.84) * mm});
            skLineSegment(sketch, "E400", {"start": v(-54.42, -101.1) * mm, "end": v(-45.05, -102.1) * mm});
            skLineSegment(sketch, "E401", {"start": v(-55.56, -105.5) * mm, "end": v(-54.42, -101.1) * mm});
            skLineSegment(sketch, "E402", {"start": v(-63.05, -103.57) * mm, "end": v(-55.56, -105.5) * mm});
            skLineSegment(sketch, "E403", {"start": v(-66.66, -107.57) * mm, "end": v(-63.05, -103.57) * mm});
            skLineSegment(sketch, "E404", {"start": v(-72.5, -104.66) * mm, "end": v(-66.66, -107.57) * mm});
            skLineSegment(sketch, "E405", {"start": v(-79.74, -107.25) * mm, "end": v(-72.5, -104.66) * mm});
            skLineSegment(sketch, "E406", {"start": v(-82.97, -103.36) * mm, "end": v(-79.74, -107.25) * mm});
            skLineSegment(sketch, "E407", {"start": v(-89.43, -104.75) * mm, "end": v(-82.97, -103.36) * mm});
            skLineSegment(sketch, "E408", {"start": v(-92.66, -100.86) * mm, "end": v(-89.43, -104.75) * mm});
            skLineSegment(sketch, "E409", {"start": v(-101.17, -101.72) * mm, "end": v(-92.66, -100.86) * mm});
            skLineSegment(sketch, "E410", {"start": v(-113.74, -108.81) * mm, "end": v(-101.17, -101.72) * mm});
            skLineSegment(sketch, "E411", {"start": v(-115.2, -106.24) * mm, "end": v(-113.74, -108.81) * mm});
            skLineSegment(sketch, "E412", {"start": v(-109.08, -102.79) * mm, "end": v(-115.2, -106.24) * mm});
            skLineSegment(sketch, "E413", {"start": v(-110.6, -100.09) * mm, "end": v(-109.08, -102.79) * mm});
            skLineSegment(sketch, "E414", {"start": v(-116.72, -103.54) * mm, "end": v(-110.6, -100.09) * mm});
            skLineSegment(sketch, "E415", {"start": v(-117.93, -101.39) * mm, "end": v(-116.72, -103.54) * mm});
            skLineSegment(sketch, "E416", {"start": v(-116.97, -97.64) * mm, "end": v(-117.93, -101.39) * mm});
            skLineSegment(sketch, "E417", {"start": v(-108.74, -96.71) * mm, "end": v(-116.97, -97.64) * mm});
            skLineSegment(sketch, "E418", {"start": v(-107.15, -90.56) * mm, "end": v(-108.74, -96.71) * mm});
            skLineSegment(sketch, "E419", {"start": v(-101.37, -92.05) * mm, "end": v(-107.15, -90.56) * mm});
            skLineSegment(sketch, "E420", {"start": v(-93.74, -91.42) * mm, "end": v(-97.3, -87.92) * mm});
            skLineSegment(sketch, "E421", {"start": v(-85.22, -88.45) * mm, "end": v(-93.74, -91.42) * mm});
            skLineSegment(sketch, "E422", {"start": v(-82.99, -91.61) * mm, "end": v(-85.22, -88.45) * mm});
            skLineSegment(sketch, "E423", {"start": v(-76.85, -90.6) * mm, "end": v(-82.99, -91.61) * mm});
            skLineSegment(sketch, "E424", {"start": v(-74.62, -93.77) * mm, "end": v(-76.85, -90.6) * mm});
            skLineSegment(sketch, "E425", {"start": v(-71.13, -92.09) * mm, "end": v(-74.62, -93.77) * mm});
            skLineSegment(sketch, "E426", {"start": v(-67.16, -93.11) * mm, "end": v(-71.13, -92.09) * mm});
            skLineSegment(sketch, "E427", {"start": v(-60.18, -88.8) * mm, "end": v(-67.16, -93.11) * mm});
            skLineSegment(sketch, "E428", {"start": v(-63.03, -78.84) * mm, "end": v(-60.18, -88.8) * mm});
            skLineSegment(sketch, "E429", {"start": v(-56.19, -80.61) * mm, "end": v(-63.03, -78.84) * mm});
            skLineSegment(sketch, "E430", {"start": v(-55.41, -77.6) * mm, "end": v(-56.19, -80.61) * mm});
            skLineSegment(sketch, "E431", {"start": v(-64.03, -75.38) * mm, "end": v(-55.41, -77.6) * mm});
            skLineSegment(sketch, "E432", {"start": v(-66.73, -66.07) * mm, "end": v(-64.03, -75.38) * mm});
            skLineSegment(sketch, "E433", {"start": v(-60.34, -67.72) * mm, "end": v(-66.73, -66.07) * mm});
            skLineSegment(sketch, "E434", {"start": v(-59.56, -64.72) * mm, "end": v(-60.34, -67.72) * mm});
            skLineSegment(sketch, "E435", {"start": v(-67.73, -62.61) * mm, "end": v(-59.56, -64.72) * mm});
            skLineSegment(sketch, "E436", {"start": v(-63.54, -54.35) * mm, "end": v(-70.66, -52.52) * mm});
            skLineSegment(sketch, "E437", {"start": v(-62.77, -51.35) * mm, "end": v(-63.54, -54.35) * mm});
            skLineSegment(sketch, "E438", {"start": v(-71.66, -49.06) * mm, "end": v(-62.77, -51.35) * mm});
            skLineSegment(sketch, "E439", {"start": v(-73.46, -42.85) * mm, "end": v(-71.66, -49.06) * mm});
            skLineSegment(sketch, "E440", {"start": v(-79.21, -38.68) * mm, "end": v(-73.46, -42.85) * mm});
            skLineSegment(sketch, "E441", {"start": v(-79.59, -38.26) * mm, "end": v(-79.21, -38.68) * mm});
            skLineSegment(sketch, "E442", {"start": v(-79.78, -37.74) * mm, "end": v(-79.59, -38.26) * mm});
            skLineSegment(sketch, "E443", {"start": v(-79.75, -37.18) * mm, "end": v(-79.78, -37.74) * mm});
            skLineSegment(sketch, "E444", {"start": v(-79.21, -35.11) * mm, "end": v(-79.75, -37.18) * mm});
            skLineSegment(sketch, "E445", {"start": v(-78.74, -34.12) * mm, "end": v(-79.21, -35.11) * mm});
            skLineSegment(sketch, "E446", {"start": v(-77.92, -33.39) * mm, "end": v(-78.74, -34.12) * mm});
            skLineSegment(sketch, "E447", {"start": v(-76.88, -33.03) * mm, "end": v(-77.92, -33.39) * mm});
            skLineSegment(sketch, "E448", {"start": v(-75.78, -33.09) * mm, "end": v(-76.88, -33.03) * mm});
            skLineSegment(sketch, "E449", {"start": v(-71.24, -34.26) * mm, "end": v(-75.78, -33.09) * mm});
            skLineSegment(sketch, "E450", {"start": v(-70.1, -29.85) * mm, "end": v(-71.24, -34.26) * mm});
            skLineSegment(sketch, "E451", {"start": v(-76, -28.33) * mm, "end": v(-70.1, -29.85) * mm});
            skLineSegment(sketch, "E452", {"start": v(-76.64, -27.97) * mm, "end": v(-76, -28.33) * mm});
            skLineSegment(sketch, "E453", {"start": v(-77.01, -27.34) * mm, "end": v(-76.64, -27.97) * mm});
            skLineSegment(sketch, "E454", {"start": v(-77.02, -26.61) * mm, "end": v(-77.01, -27.34) * mm});
            skLineSegment(sketch, "E455", {"start": v(-76.26, -23.9) * mm, "end": v(-77.02, -26.61) * mm});
            skLineSegment(sketch, "E456", {"start": v(61.28, -41.9) * mm, "end": v(63.46, -35.23) * mm});
            skLineSegment(sketch, "E457", {"start": v(52.6, -39.92) * mm, "end": v(61.28, -41.9) * mm});
            skLineSegment(sketch, "E458", {"start": v(51.9, -42.94) * mm, "end": v(52.6, -39.92) * mm});
            skLineSegment(sketch, "E459", {"start": v(60.3, -44.86) * mm, "end": v(51.9, -42.94) * mm});
            skLineSegment(sketch, "E460", {"start": v(58.5, -50.39) * mm, "end": v(60.3, -44.86) * mm});
            skLineSegment(sketch, "E461", {"start": v(51.39, -50.66) * mm, "end": v(58.5, -50.39) * mm});
            skLineSegment(sketch, "E462", {"start": v(26.86, 71.53) * mm, "end": v(23.45, 72.05) * mm});
            skLineSegment(sketch, "E463", {"start": v(-50.05, 16.1) * mm, "end": v(-50.26, 13.88) * mm});
            skLineSegment(sketch, "E464", {"start": v(55.73, -28.2) * mm, "end": v(53.26, -27.63) * mm});
            skLineSegment(sketch, "E465", {"start": v(-52.82, -29.96) * mm, "end": v(-54.12, -31.66) * mm});
            skLineSegment(sketch, "E466", {"start": v(48.9, -50.11) * mm, "end": v(51.39, -50.66) * mm});
            skLineSegment(sketch, "E467", {"start": v(-40.04, 52.33) * mm, "end": v(-40.32, 48.76) * mm});
            skLineSegment(sketch, "E468", {"start": v(-87.36, -77.1) * mm, "end": v(-91, -78.34) * mm});
            skLineSegment(sketch, "E469", {"start": v(-97.07, -78.98) * mm, "end": v(-91, -78.34) * mm});
            skLineSegment(sketch, "E470", {"start": v(-106.77, -77.1) * mm, "end": v(-103.13, -78.34) * mm});
            skLineSegment(sketch, "E471", {"start": v(-97.07, -78.98) * mm, "end": v(-103.13, -78.34) * mm});
            skLineSegment(sketch, "E472", {"start": v(-98.62, -55.05) * mm, "end": v(-98.62, -63.25) * mm});
            skLineSegment(sketch, "E473", {"start": v(-103.97, -55.05) * mm, "end": v(-98.62, -55.05) * mm});
            skLineSegment(sketch, "E474", {"start": v(-103.98, -63.23) * mm, "end": v(-103.97, -55.05) * mm});
            skLineSegment(sketch, "E475", {"start": v(-107.09, -63.23) * mm, "end": v(-103.98, -63.23) * mm});
            skLineSegment(sketch, "E476", {"start": v(-107.09, -55.05) * mm, "end": v(-107.09, -63.23) * mm});
            skLineSegment(sketch, "E477", {"start": v(-117.86, -55.05) * mm, "end": v(-107.09, -55.05) * mm});
            skLineSegment(sketch, "E478", {"start": v(-119.1, -55.83) * mm, "end": v(-117.86, -55.05) * mm});
            skLineSegment(sketch, "E479", {"start": v(-122.92, -71.63) * mm, "end": v(-118.65, -63.94) * mm});
            skLineSegment(sketch, "E480", {"start": v(-122.48, -74.71) * mm, "end": v(-122.92, -71.63) * mm});
            skLineSegment(sketch, "E481", {"start": v(-120.88, -75.84) * mm, "end": v(-122.48, -74.71) * mm});
            skLineSegment(sketch, "E482", {"start": v(-117.78, -76.12) * mm, "end": v(-120.88, -75.84) * mm});
            skLineSegment(sketch, "E483", {"start": v(-115.3, -66.37) * mm, "end": v(-117.78, -76.12) * mm});
            skLineSegment(sketch, "E484", {"start": v(-112.3, -67.13) * mm, "end": v(-115.3, -66.37) * mm});
            skLineSegment(sketch, "E485", {"start": v(-114.65, -76.4) * mm, "end": v(-112.3, -67.13) * mm});
            skLineSegment(sketch, "E486", {"start": v(-106.77, -77.1) * mm, "end": v(-114.65, -76.4) * mm});
            skLineSegment(sketch, "E487", {"start": v(-85.94, 96.9) * mm, "end": v(-83.17, 98.27) * mm});
            skLineSegment(sketch, "E488", {"start": v(-90.77, 107.97) * mm, "end": v(-90.25, 108.36) * mm});
            skLineSegment(sketch, "E489", {"start": v(-91.05, 107.38) * mm, "end": v(-90.77, 107.97) * mm});
            skLineSegment(sketch, "E490", {"start": v(-92.74, 104.25) * mm, "end": v(-91.05, 107.38) * mm});
            skLineSegment(sketch, "E491", {"start": v(-92.76, 103.76) * mm, "end": v(-92.74, 104.25) * mm});
            skLineSegment(sketch, "E492", {"start": v(-92.62, 103.3) * mm, "end": v(-92.76, 103.76) * mm});
            skLineSegment(sketch, "E493", {"start": v(-91.1, 97.87) * mm, "end": v(-92.62, 103.3) * mm});
            skLineSegment(sketch, "E494", {"start": v(-96.34, 89.38) * mm, "end": v(-91.1, 97.87) * mm});
            skLineSegment(sketch, "E495", {"start": v(-105.58, 86.65) * mm, "end": v(-96.34, 89.38) * mm});
            skLineSegment(sketch, "E496", {"start": v(-103.03, 79.8) * mm, "end": v(-99.98, 80.33) * mm});
            skLineSegment(sketch, "E497", {"start": v(-107.81, 75.45) * mm, "end": v(-107.74, 81.99) * mm});
            skLineSegment(sketch, "E498", {"start": v(-103.52, 72.84) * mm, "end": v(-107.81, 75.45) * mm});
            skLineSegment(sketch, "E499", {"start": v(-98.33, 74.35) * mm, "end": v(-98.92, 74.18) * mm});
            skLineSegment(sketch, "E500", {"start": v(-95.8, 73.8) * mm, "end": v(-98.33, 74.35) * mm});
            skLineSegment(sketch, "E501", {"start": v(-87.54, 61.14) * mm, "end": v(-95.8, 73.8) * mm});
            skLineSegment(sketch, "E502", {"start": v(-75.27, 57.62) * mm, "end": v(-78.12, 55.7) * mm});
            skLineSegment(sketch, "E503", {"start": v(-87.49, 87.7) * mm, "end": v(-88.01, 87.25) * mm});
            skLineSegment(sketch, "E504", {"start": v(-82.65, 90.25) * mm, "end": v(-87.49, 87.7) * mm});
            skLineSegment(sketch, "E505", {"start": v(-85.94, 96.9) * mm, "end": v(-82.65, 90.25) * mm});
            skLineSegment(sketch, "E506", {"start": v(-77.57, 61.25) * mm, "end": v(-75.27, 57.62) * mm});
            skLineSegment(sketch, "E507", {"start": v(-77.57, 61.25) * mm, "end": v(-85.8, 71.45) * mm});
            skLineSegment(sketch, "E508", {"start": v(-85.8, 71.45) * mm, "end": v(-90.56, 79.79) * mm});
            skLineSegment(sketch, "E509", {"start": v(-90.56, 79.79) * mm, "end": v(-88.01, 87.25) * mm});
            skLineSegment(sketch, "E510", {"start": v(-74.24, 94.08) * mm, "end": v(-66.57, 91.46) * mm});
            skLineSegment(sketch, "E511", {"start": v(-66.57, 91.46) * mm, "end": v(-58.37, 66) * mm});
            skLineSegment(sketch, "E512", {"start": v(105.98, 34.97) * mm, "end": v(104.89, 41.54) * mm});
            skLineSegment(sketch, "E513", {"start": v(101.64, 42.16) * mm, "end": v(93.23, 43.75) * mm});
            skLineSegment(sketch, "E514", {"start": v(102.92, 34.46) * mm, "end": v(101.64, 42.16) * mm});
            skLineSegment(sketch, "E515", {"start": v(-61.49, 99.4) * mm, "end": v(-57.28, 94.9) * mm});
            skLineSegment(sketch, "E516", {"start": v(-54.72, 96.7) * mm, "end": v(-53.38, 97.7) * mm});
            skLineSegment(sketch, "E517", {"start": v(-59.22, 101.52) * mm, "end": v(-54.72, 96.7) * mm});
            skLineSegment(sketch, "E518", {"start": v(-57.28, 94.9) * mm, "end": v(-57.23, 94.84) * mm});
            skLineSegment(sketch, "E519", {"start": v(-63.15, 107.68) * mm, "end": v(-70.9, 102) * mm});
            skLineSegment(sketch, "E520", {"start": v(-58.15, 106.62) * mm, "end": v(-63.15, 107.68) * mm});
            skLineSegment(sketch, "E521", {"start": v(-99.98, 80.33) * mm, "end": v(-98.92, 74.18) * mm});
            skLineSegment(sketch, "E522", {"start": v(-101.92, 73.3) * mm, "end": v(-103.52, 72.84) * mm});
            skLineSegment(sketch, "E523", {"start": v(-103.03, 79.8) * mm, "end": v(-101.92, 73.3) * mm});
            skLineSegment(sketch, "E524", {"start": v(-107.74, 81.99) * mm, "end": v(-105.58, 86.65) * mm});
            skLineSegment(sketch, "E525", {"start": v(129.2, -6.01) * mm, "end": v(119.25, -0.4) * mm});
            skLineSegment(sketch, "E526", {"start": v(43, -0.47) * mm, "end": v(43.68, -1) * mm});
            skLineSegment(sketch, "E527", {"start": v(41.5, -4.36) * mm, "end": v(43, -0.47) * mm});
            skLineSegment(sketch, "E528", {"start": v(39.7, 0.32) * mm, "end": v(41.5, -4.36) * mm});
            skLineSegment(sketch, "E529", {"start": v(38.38, -5.14) * mm, "end": v(39.7, 0.32) * mm});
            skLineSegment(sketch, "E530", {"start": v(36.9, -1.55) * mm, "end": v(38.38, -5.14) * mm});
            skLineSegment(sketch, "E531", {"start": v(36.9, 1.95) * mm, "end": v(36.9, -1.55) * mm});
            skLineSegment(sketch, "E532", {"start": v(35.2, 0.43) * mm, "end": v(36.9, 1.95) * mm});
            skLineSegment(sketch, "E533", {"start": v(33.4, -4.36) * mm, "end": v(35.2, 0.43) * mm});
            skLineSegment(sketch, "E534", {"start": v(32.39, -1) * mm, "end": v(33.4, -4.36) * mm});
            skLineSegment(sketch, "E535", {"start": v(32.07, 3.04) * mm, "end": v(32.39, -1) * mm});
            skLineSegment(sketch, "E536", {"start": v(30.78, -1.85) * mm, "end": v(32.07, 3.04) * mm});
            skLineSegment(sketch, "E537", {"start": v(27.71, 4.76) * mm, "end": v(30.78, -1.85) * mm});
            skLineSegment(sketch, "E538", {"start": v(28.96, 13.17) * mm, "end": v(27.09, 9.12) * mm});
            skLineSegment(sketch, "E539", {"start": v(33.32, 16.13) * mm, "end": v(28.96, 13.17) * mm});
            skLineSegment(sketch, "E540", {"start": v(35.52, 16.65) * mm, "end": v(33.32, 16.13) * mm});
            skLineSegment(sketch, "E541", {"start": v(31.3, 12.5) * mm, "end": v(35.83, 14.8) * mm});
            skLineSegment(sketch, "E542", {"start": v(29.25, 10.3) * mm, "end": v(31.3, 12.5) * mm});
            skLineSegment(sketch, "E543", {"start": v(30.48, 9.16) * mm, "end": v(29.25, 10.3) * mm});
            skLineSegment(sketch, "E544", {"start": v(32.34, 9.16) * mm, "end": v(30.48, 9.16) * mm});
            skLineSegment(sketch, "E545", {"start": v(38.02, 13.3) * mm, "end": v(32.34, 9.16) * mm});
            skLineSegment(sketch, "E546", {"start": v(38.82, 14.2) * mm, "end": v(38.02, 13.3) * mm});
            skLineSegment(sketch, "E547", {"start": v(38.82, 15.3) * mm, "end": v(38.82, 14.2) * mm});
            skLineSegment(sketch, "E548", {"start": v(36.63, 14.93) * mm, "end": v(38.82, 15.3) * mm});
            skLineSegment(sketch, "E549", {"start": v(37.92, 17.22) * mm, "end": v(36.31, 16.84) * mm});
            skLineSegment(sketch, "E550", {"start": v(38.46, 18.08) * mm, "end": v(37.92, 17.22) * mm});
            skLineSegment(sketch, "E551", {"start": v(43.02, 18.08) * mm, "end": v(38.46, 18.08) * mm});
            skLineSegment(sketch, "E552", {"start": v(46.49, 19.71) * mm, "end": v(43.02, 18.08) * mm});
            skLineSegment(sketch, "E553", {"start": v(48.98, 19.01) * mm, "end": v(46.49, 19.71) * mm});
            skLineSegment(sketch, "E554", {"start": v(51.47, 21.12) * mm, "end": v(48.98, 19.01) * mm});
            skLineSegment(sketch, "E555", {"start": v(57.63, 21.12) * mm, "end": v(51.47, 21.12) * mm});
            skLineSegment(sketch, "E556", {"start": v(61.2, 22.38) * mm, "end": v(57.63, 21.12) * mm});
            skLineSegment(sketch, "E557", {"start": v(52.49, 16.78) * mm, "end": v(61.2, 19.6) * mm});
            skLineSegment(sketch, "E558", {"start": v(51.33, 13.95) * mm, "end": v(52.49, 16.78) * mm});
            skLineSegment(sketch, "E559", {"start": v(51.33, 11.52) * mm, "end": v(51.33, 13.95) * mm});
            skLineSegment(sketch, "E560", {"start": v(51.81, 10) * mm, "end": v(51.33, 11.52) * mm});
            skLineSegment(sketch, "E561", {"start": v(54.52, 8.76) * mm, "end": v(51.81, 10) * mm});
            skLineSegment(sketch, "E562", {"start": v(58.91, 9.56) * mm, "end": v(54.52, 8.76) * mm});
            skLineSegment(sketch, "E563", {"start": v(61.62, 11.52) * mm, "end": v(58.91, 9.56) * mm});
            skLineSegment(sketch, "E564", {"start": v(61.62, 14.55) * mm, "end": v(61.62, 11.52) * mm});
            skLineSegment(sketch, "E565", {"start": v(61.02, 15.55) * mm, "end": v(61.62, 14.55) * mm});
            skLineSegment(sketch, "E566", {"start": v(61.98, 17.74) * mm, "end": v(61.02, 15.55) * mm});
            skLineSegment(sketch, "E567", {"start": v(71.34, 27.35) * mm, "end": v(69.08, 25.17) * mm});
            skLineSegment(sketch, "E568", {"start": v(80.38, 25.17) * mm, "end": v(71.34, 27.35) * mm});
            skLineSegment(sketch, "E569", {"start": v(87.93, 20.42) * mm, "end": v(80.38, 25.17) * mm});
            skLineSegment(sketch, "E570", {"start": v(90.66, 15.04) * mm, "end": v(87.93, 20.42) * mm});
            skLineSegment(sketch, "E571", {"start": v(86.06, 10.6) * mm, "end": v(90.66, 15.04) * mm});
            skLineSegment(sketch, "E572", {"start": v(84.04, 11.77) * mm, "end": v(86.06, 10.6) * mm});
            skLineSegment(sketch, "E573", {"start": v(82.01, 3.43) * mm, "end": v(84.04, 11.77) * mm});
            skLineSegment(sketch, "E574", {"start": v(78.96, 3.38) * mm, "end": v(82.01, 3.43) * mm});
            skLineSegment(sketch, "E575", {"start": v(75.46, 11.72) * mm, "end": v(78.96, 3.38) * mm});
            skLineSegment(sketch, "E576", {"start": v(72.62, 10.53) * mm, "end": v(75.46, 11.72) * mm});
            skLineSegment(sketch, "E577", {"start": v(75.87, 2.79) * mm, "end": v(72.62, 10.53) * mm});
            skLineSegment(sketch, "E578", {"start": v(74.3, 1.95) * mm, "end": v(75.87, 2.79) * mm});
            skLineSegment(sketch, "E579", {"start": v(62.46, 1.02) * mm, "end": v(65.5, 1.95) * mm});
            skLineSegment(sketch, "E580", {"start": v(60.35, 3.98) * mm, "end": v(62.46, 1.02) * mm});
            skLineSegment(sketch, "E581", {"start": v(54.2, 3.43) * mm, "end": v(60.35, 3.98) * mm});
            skLineSegment(sketch, "E582", {"start": v(51.4, 1.95) * mm, "end": v(54.2, 3.43) * mm});
            skLineSegment(sketch, "E583", {"start": v(51.4, -1.55) * mm, "end": v(51.4, 1.95) * mm});
            skLineSegment(sketch, "E584", {"start": v(49.06, 1.95) * mm, "end": v(51.4, -1.55) * mm});
            skLineSegment(sketch, "E585", {"start": v(46.02, 1.95) * mm, "end": v(49.06, 1.95) * mm});
            skLineSegment(sketch, "E586", {"start": v(45.12, -4.36) * mm, "end": v(46.02, 1.95) * mm});
            skLineSegment(sketch, "E587", {"start": v(43.68, -1) * mm, "end": v(45.12, -4.36) * mm});
            skLineSegment(sketch, "E588", {"start": v(59.96, -18.36) * mm, "end": v(65.2, -18.36) * mm});
            skLineSegment(sketch, "E589", {"start": v(63.08, -14.71) * mm, "end": v(59.96, -15.54) * mm});
            skLineSegment(sketch, "E590", {"start": v(68.5, -9.98) * mm, "end": v(63.08, -14.71) * mm});
            skLineSegment(sketch, "E591", {"start": v(68.5, -8) * mm, "end": v(68.5, -9.98) * mm});
            skLineSegment(sketch, "E592", {"start": v(66.6, -8) * mm, "end": v(68.5, -8) * mm});
            skLineSegment(sketch, "E593", {"start": v(62, -9.98) * mm, "end": v(66.6, -8) * mm});
            skLineSegment(sketch, "E594", {"start": v(53.22, -12.36) * mm, "end": v(62, -9.98) * mm});
            skLineSegment(sketch, "E595", {"start": v(52.32, -13.56) * mm, "end": v(53.22, -12.36) * mm});
            skLineSegment(sketch, "E596", {"start": v(54.96, -15.54) * mm, "end": v(52.32, -13.56) * mm});
            skLineSegment(sketch, "E597", {"start": v(59.06, -15.54) * mm, "end": v(54.96, -15.54) * mm});
            skLineSegment(sketch, "E598", {"start": v(38.61, -19.35) * mm, "end": v(46.56, -18.36) * mm});
            skLineSegment(sketch, "E599", {"start": v(34.87, -18.26) * mm, "end": v(38.61, -19.35) * mm});
            skLineSegment(sketch, "E600", {"start": v(33.08, -15.28) * mm, "end": v(34.87, -18.26) * mm});
            skLineSegment(sketch, "E601", {"start": v(33.08, -15.28) * mm, "end": v(32.54, -13.28) * mm});
            skLineSegment(sketch, "E602", {"start": v(32.54, -9.23) * mm, "end": v(32.54, -13.28) * mm});
            skLineSegment(sketch, "E603", {"start": v(33.7, -10.78) * mm, "end": v(32.54, -9.23) * mm});
            skLineSegment(sketch, "E604", {"start": v(34.87, -11.2) * mm, "end": v(33.7, -10.78) * mm});
            skLineSegment(sketch, "E605", {"start": v(36.58, -12.18) * mm, "end": v(34.87, -11.2) * mm});
            skLineSegment(sketch, "E606", {"start": v(35.96, -9.23) * mm, "end": v(36.58, -12.18) * mm});
            skLineSegment(sketch, "E607", {"start": v(36.58, -7.43) * mm, "end": v(35.96, -9.23) * mm});
            skLineSegment(sketch, "E608", {"start": v(38.61, -10.78) * mm, "end": v(36.58, -7.43) * mm});
            skLineSegment(sketch, "E609", {"start": v(39.94, -7.43) * mm, "end": v(38.61, -10.78) * mm});
            skLineSegment(sketch, "E610", {"start": v(41.5, -10.78) * mm, "end": v(39.94, -7.43) * mm});
            skLineSegment(sketch, "E611", {"start": v(42.59, -8.13) * mm, "end": v(41.5, -10.78) * mm});
            skLineSegment(sketch, "E612", {"start": v(44.64, -10.78) * mm, "end": v(42.59, -8.13) * mm});
            skLineSegment(sketch, "E613", {"start": v(44.94, -7.43) * mm, "end": v(44.64, -10.78) * mm});
            skLineSegment(sketch, "E614", {"start": v(46.56, -9.9) * mm, "end": v(44.94, -7.43) * mm});
            skLineSegment(sketch, "E615", {"start": v(47.8, -5.88) * mm, "end": v(46.56, -9.9) * mm});
            skLineSegment(sketch, "E616", {"start": v(49.2, -8.45) * mm, "end": v(47.8, -5.88) * mm});
            skLineSegment(sketch, "E617", {"start": v(56.24, -4.61) * mm, "end": v(49.2, -8.45) * mm});
            skLineSegment(sketch, "E618", {"start": v(60.58, -4) * mm, "end": v(56.24, -4.61) * mm});
            skLineSegment(sketch, "E619", {"start": v(64.76, -1.78) * mm, "end": v(60.58, -4) * mm});
            skLineSegment(sketch, "E620", {"start": v(84.2, -0.6) * mm, "end": v(76.98, 0.34) * mm});
            skLineSegment(sketch, "E621", {"start": v(84.53, 1.9) * mm, "end": v(84.2, -0.6) * mm});
            skLineSegment(sketch, "E622", {"start": v(86.89, 0.96) * mm, "end": v(84.53, 1.9) * mm});
            skLineSegment(sketch, "E623", {"start": v(88.2, -4) * mm, "end": v(86.89, 0.96) * mm});
            skLineSegment(sketch, "E624", {"start": v(82.06, -8.86) * mm, "end": v(88.2, -4) * mm});
            skLineSegment(sketch, "E625", {"start": v(79.9, -4.12) * mm, "end": v(82.06, -8.86) * mm});
            skLineSegment(sketch, "E626", {"start": v(77.1, -5.4) * mm, "end": v(79.9, -4.12) * mm});
            skLineSegment(sketch, "E627", {"start": v(79.17, -9.94) * mm, "end": v(77.1, -5.4) * mm});
            skLineSegment(sketch, "E628", {"start": v(76.98, -10.44) * mm, "end": v(79.17, -9.94) * mm});
            skLineSegment(sketch, "E629", {"start": v(65.2, -18.36) * mm, "end": v(76.98, -10.44) * mm});
            skLineSegment(sketch, "E630", {"start": v(26.86, 71.53) * mm, "end": v(31.26, 73.6) * mm});
            skLineSegment(sketch, "E631", {"start": v(32.98, 74.41) * mm, "end": v(36.44, 76.04) * mm});
            skLineSegment(sketch, "E632", {"start": v(-78.12, 55.7) * mm, "end": v(-81.33, 57.56) * mm});
            skLineSegment(sketch, "E633", {"start": v(-83.06, 58.56) * mm, "end": v(-87.54, 61.14) * mm});
            skLineSegment(sketch, "E634", {"start": v(76.34, 35.85) * mm, "end": v(78.35, 35.58) * mm});
            skLineSegment(sketch, "E635", {"start": v(27.09, 9.12) * mm, "end": v(27.36, 7.22) * mm});
            skLineSegment(sketch, "E636", {"start": v(-53.83, 22.37) * mm, "end": v(-52.44, 25.52) * mm});
            skLineSegment(sketch, "E637", {"start": v(-118.65, -63.94) * mm, "end": v(-118.9, -59.19) * mm});
            skLineSegment(sketch, "E638", {"start": v(-119.02, -57.07) * mm, "end": v(-119.1, -55.83) * mm});
            skLineSegment(sketch, "E639", {"start": v(-80.53, -0.02) * mm, "end": v(-78.33, -0.02) * mm});
            skLineSegment(sketch, "E640", {"start": v(-76.28, -0.02) * mm, "end": v(-72.85, -0.02) * mm});
            skLineSegment(sketch, "E641", {"start": v(46.56, -18.36) * mm, "end": v(51.06, -18.36) * mm});
            skLineSegment(sketch, "E642", {"start": v(76.98, 0.34) * mm, "end": v(71.44, -0.62) * mm});
            skLineSegment(sketch, "E643", {"start": v(69.09, -1.03) * mm, "end": v(64.76, -1.78) * mm});
            skLineSegment(sketch, "E644", {"start": v(65.5, 1.95) * mm, "end": v(68.83, 1.95) * mm});
            skLineSegment(sketch, "E645", {"start": v(71.16, 1.95) * mm, "end": v(74.3, 1.95) * mm});
            skLineSegment(sketch, "E646", {"start": v(123.6, 28.83) * mm, "end": v(120.1, 35.72) * mm});
            skLineSegment(sketch, "E647", {"start": v(-70.66, -52.52) * mm, "end": v(-67.73, -62.61) * mm});
            skLineSegment(sketch, "E648", {"start": v(-51.16, -16.89) * mm, "end": v(-56.1, -15.61) * mm});
            skLineSegment(sketch, "E649", {"start": v(125.22, -44.36) * mm, "end": v(127.71, -43) * mm});
            skLineSegment(sketch, "E650", {"start": v(69.08, 25.17) * mm, "end": v(67.03, 24.44) * mm});
            skLineSegment(sketch, "E651", {"start": v(18.08, -38.98) * mm, "end": v(41.67, -47.5) * mm});
            skLineSegment(sketch, "E652", {"start": v(43.7, -48.24) * mm, "end": v(48.9, -50.11) * mm});
            skLineSegment(sketch, "E653", {"start": v(-45.64, 44.43) * mm, "end": v(-44.43, 45.1) * mm});
            skLineSegment(sketch, "E654", {"start": v(-42.16, 46.35) * mm, "end": v(-40.32, 47.37) * mm});
            skLineSegment(sketch, "E655", {"start": v(-99.05, -89.69) * mm, "end": v(-101.37, -92.05) * mm});
            skLineSegment(sketch, "E656", {"start": v(-66.81, -14) * mm, "end": v(-68.44, -14.3) * mm});
            skLineSegment(sketch, "E657", {"start": v(75.97, -24.28) * mm, "end": v(74.98, -24.52) * mm});
            skLineSegment(sketch, "E658", {"start": v(72.32, -25.19) * mm, "end": v(66.5, -26.64) * mm});
            skLineSegment(sketch, "E659", {"start": v(122.2, 21.13) * mm, "end": v(122.84, 24.65) * mm});
            skLineSegment(sketch, "E660", {"start": v(123.24, 26.83) * mm, "end": v(123.6, 28.83) * mm});
            skLineSegment(sketch, "E661", {"start": v(-94.8, 31.36) * mm, "end": v(-93.45, 29.23) * mm});
            skLineSegment(sketch, "E662", {"start": v(72.66, 47.93) * mm, "end": v(70.43, 47.22) * mm});
            skLineSegment(sketch, "E663", {"start": v(74.12, 36.16) * mm, "end": v(76.34, 35.85) * mm});
            skLineSegment(sketch, "E664", {"start": v(-81.33, 57.56) * mm, "end": v(-83.06, 58.56) * mm});
            skLineSegment(sketch, "E665", {"start": v(123.24, 26.83) * mm, "end": v(122.84, 24.65) * mm});
            skLineSegment(sketch, "E666", {"start": v(-48.38, -17.6) * mm, "end": v(-51.16, -16.89) * mm});
            skLineSegment(sketch, "E667", {"start": v(72.32, -25.19) * mm, "end": v(75.47, -24.4) * mm});
            skLineSegment(sketch, "E668", {"start": v(-66.81, -14) * mm, "end": v(-64.24, -13.51) * mm});
            skLineSegment(sketch, "E669", {"start": v(-97.3, -87.92) * mm, "end": v(-99.05, -89.69) * mm});
            skLineSegment(sketch, "E670", {"start": v(43.7, -48.24) * mm, "end": v(41.67, -47.5) * mm});
            skLineSegment(sketch, "E671", {"start": v(-44.43, 45.1) * mm, "end": v(-42.16, 46.35) * mm});
            skLineSegment(sketch, "E672", {"start": v(127.71, -43) * mm, "end": v(130.25, -41.62) * mm});
            skLineSegment(sketch, "E673", {"start": v(61.2, 22.38) * mm, "end": v(67.03, 24.44) * mm});
            skLineSegment(sketch, "E674", {"start": v(61.98, 17.74) * mm, "end": v(61.2, 19.6) * mm});
            skLineSegment(sketch, "E675", {"start": v(35.52, 16.65) * mm, "end": v(36.31, 16.84) * mm});
            skLineSegment(sketch, "E676", {"start": v(36.63, 14.93) * mm, "end": v(35.83, 14.8) * mm});
            skLineSegment(sketch, "E677", {"start": v(-51.4, 27.9) * mm, "end": v(-52.44, 25.52) * mm});
            skLineSegment(sketch, "E678", {"start": v(27.36, 7.22) * mm, "end": v(27.71, 4.76) * mm});
            skLineSegment(sketch, "E679", {"start": v(68.83, 1.95) * mm, "end": v(71.16, 1.95) * mm});
            skLineSegment(sketch, "E680", {"start": v(71.44, -0.62) * mm, "end": v(69.09, -1.03) * mm});
            skLineSegment(sketch, "E681", {"start": v(59.06, -15.54) * mm, "end": v(59.96, -15.54) * mm});
            skLineSegment(sketch, "E682", {"start": v(59.96, -18.36) * mm, "end": v(51.06, -18.36) * mm});
            skLineSegment(sketch, "E683", {"start": v(-122.8, -46.4) * mm, "end": v(-121.55, -45.3) * mm});
            skLineSegment(sketch, "E684", {"start": v(-52.85, 102.69) * mm, "end": v(-54.48, 103.9) * mm});
            skLineSegment(sketch, "E685", {"start": v(32.98, 74.41) * mm, "end": v(31.26, 73.6) * mm});
            skLineSegment(sketch, "E686", {"start": v(-78.33, -0.02) * mm, "end": v(-76.28, -0.02) * mm});
            skLineSegment(sketch, "E687", {"start": v(-119.02, -57.07) * mm, "end": v(-118.9, -59.19) * mm});
            skSolve(sketch);
        }
        {
            var Q0;
            Q0=makeQuery(id+"F0.imprint","IMPRINT",FACE,{"disambiguationData":[TD([[makeQuery(id+"F0.imprint","IMPRINT",EDGE,{"derivedFrom":sQuery(id+"F0.wireOp",EDGE,"E233")}),1.0]])]});
            var Q1;
            Q1=makeQuery(id+"F0.imprint","IMPRINT",FACE,{"disambiguationData":[TD([[makeQuery(id+"F0.imprint","IMPRINT",EDGE,{"derivedFrom":sQuery(id+"F0.wireOp",EDGE,"E185")}),1.0]])]});
            var Q2;
            Q2=makeQuery(id+"F0.imprint","IMPRINT",FACE,{"disambiguationData":[TD([[makeQuery(id+"F0.imprint","IMPRINT",EDGE,{"derivedFrom":sQuery(id+"F0.wireOp",EDGE,"E70")}),1.0]])]});
            var Q3;
            Q3=makeQuery(id+"F0.imprint","IMPRINT",FACE,{"disambiguationData":[TD([[makeQuery(id+"F0.imprint","IMPRINT",EDGE,{"derivedFrom":sQuery(id+"F0.wireOp",EDGE,"E116")}),1.0]])]});
            var Q4;
            Q4=makeQuery(id+"F0.imprint","IMPRINT",FACE,{"disambiguationData":[TD([[makeQuery(id+"F0.imprint","IMPRINT",EDGE,{"derivedFrom":sQuery(id+"F0.wireOp",EDGE,"E369")}),1.0]])]});
            var Q5;
            Q5=makeQuery(id+"F0.imprint","IMPRINT",FACE,{"disambiguationData":[TD([[makeQuery(id+"F0.imprint","IMPRINT",EDGE,{"derivedFrom":sQuery(id+"F0.wireOp",EDGE,"E131")}),1.0]])]});
            var Q6;
            Q6=makeQuery(id+"F0.imprint","IMPRINT",FACE,{"disambiguationData":[TD([[makeQuery(id+"F0.imprint","IMPRINT",EDGE,{"derivedFrom":sQuery(id+"F0.wireOp",EDGE,"E12")}),1.0]])]});
            var Q7;
            Q7=makeQuery(id+"F0.imprint","IMPRINT",FACE,{"disambiguationData":[TD([[makeQuery(id+"F0.imprint","IMPRINT",EDGE,{"derivedFrom":sQuery(id+"F0.wireOp",EDGE,"E198")}),-1.0]])]});
            var Q8;
            Q8=makeQuery(id+"F0.imprint","IMPRINT",FACE,{"disambiguationData":[TD([[makeQuery(id+"F0.imprint","IMPRINT",EDGE,{"derivedFrom":sQuery(id+"F0.wireOp",EDGE,"E526")}),1.0]])]});
            var Q9;
            Q9=makeQuery(id+"F0.imprint","IMPRINT",FACE,{"disambiguationData":[TD([[makeQuery(id+"F0.imprint","IMPRINT",EDGE,{"derivedFrom":sQuery(id+"F0.wireOp",EDGE,"E588")}),1.0]])]});
            var Q10;
            Q10=makeQuery(id+"F0.imprint","IMPRINT",FACE,{"disambiguationData":[TD([[makeQuery(id+"F0.imprint","IMPRINT",EDGE,{"derivedFrom":sQuery(id+"F0.wireOp",EDGE,"E174")}),1.0]])]});
            var Q11;
            Q11=makeQuery(id+"F0.imprint","IMPRINT",FACE,{"disambiguationData":[TD([[makeQuery(id+"F0.imprint","IMPRINT",EDGE,{"derivedFrom":sQuery(id+"F0.wireOp",EDGE,"E0")}),1.0]])]});
            extrude(context, id + "F1", {"entities" : qUnion([Q0, Q1, Q2, Q3, Q4, Q5, Q6, Q7, Q8, Q9, Q10, Q11]), "depth" : 3 * mm});
        }
    });
